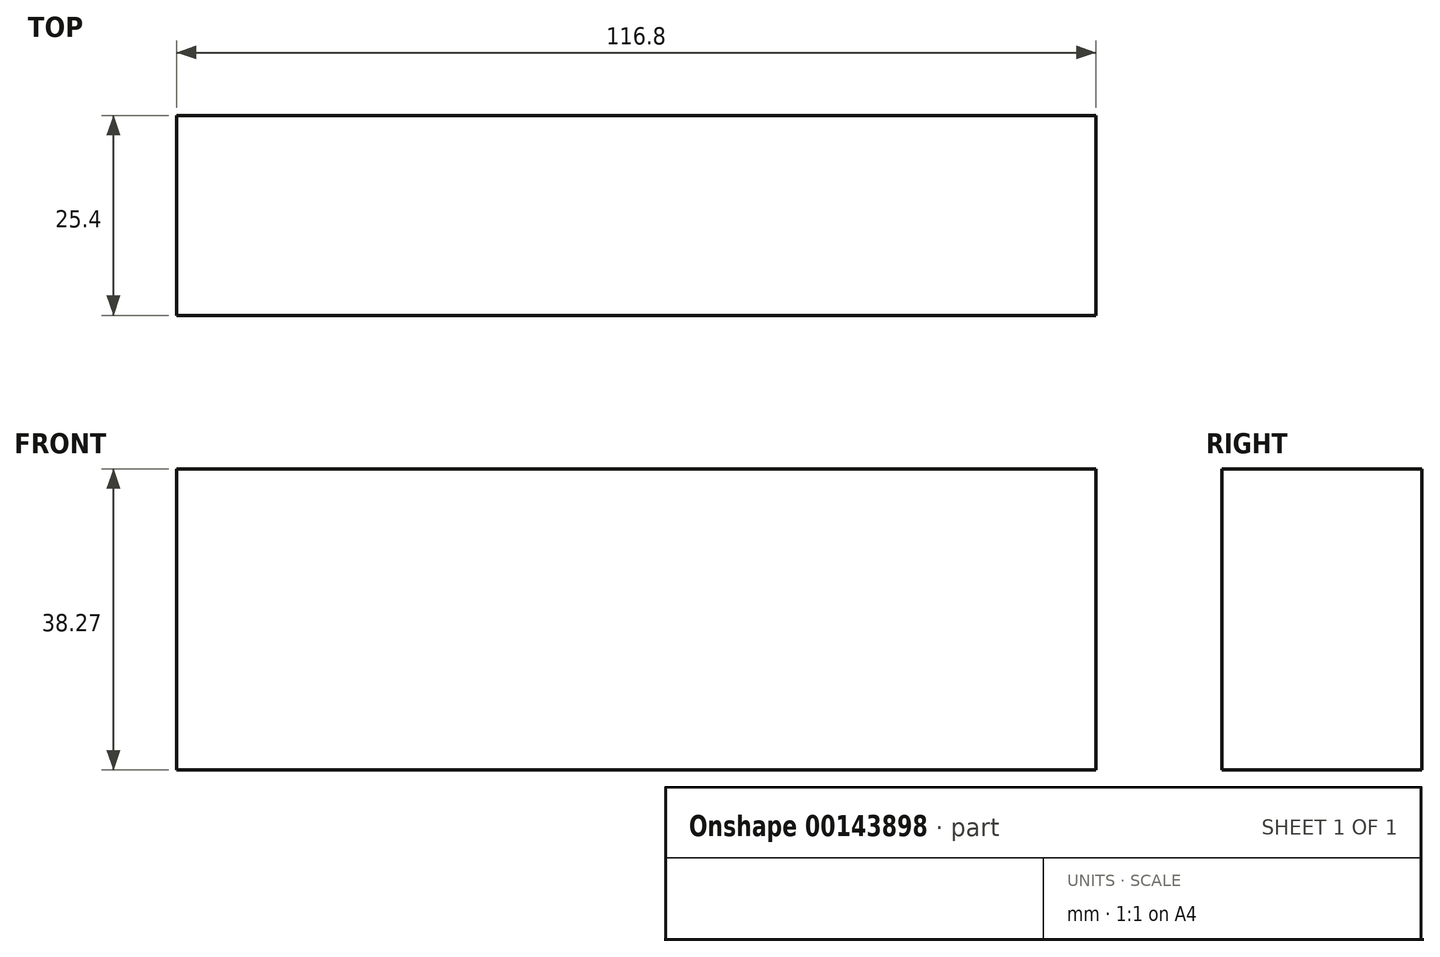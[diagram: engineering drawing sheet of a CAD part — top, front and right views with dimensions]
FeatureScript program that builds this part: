
annotation { "Feature Type Name" : "Feature", "Feature Type Description" : "" }
export const myFeature = defineFeature(function(context is Context, id is Id, definition is map)
    precondition{}
    {
        {
            var Q0;
            Q0=qCreatedBy(makeId("Front.planeOp"),FACE);
            var sketch = newSketch(context, id + "F0", { "sketchPlane" : qUnion([Q0])});
            skLineSegment(sketch, "E0.bottom", {"start": v(-116.8, 38.27) * mm, "end": v(0, 38.27) * mm});
            skLineSegment(sketch, "E0.top", {"start": v(-116.8, 0) * mm, "end": v(0, 0) * mm});
            skLineSegment(sketch, "E0.left", {"start": v(-116.8, 38.27) * mm, "end": v(-116.8, 0) * mm});
            skLineSegment(sketch, "E0.right", {"start": v(0, 38.27) * mm, "end": v(0, 0) * mm});
            skSolve(sketch);
        }
        {
            var Q0;
            Q0 = qSketchRegion(id + "F0", true);
            extrude(context, id + "F1", {"entities" : qUnion([Q0]), "depth" : 25.4 * mm});
        }
    });
